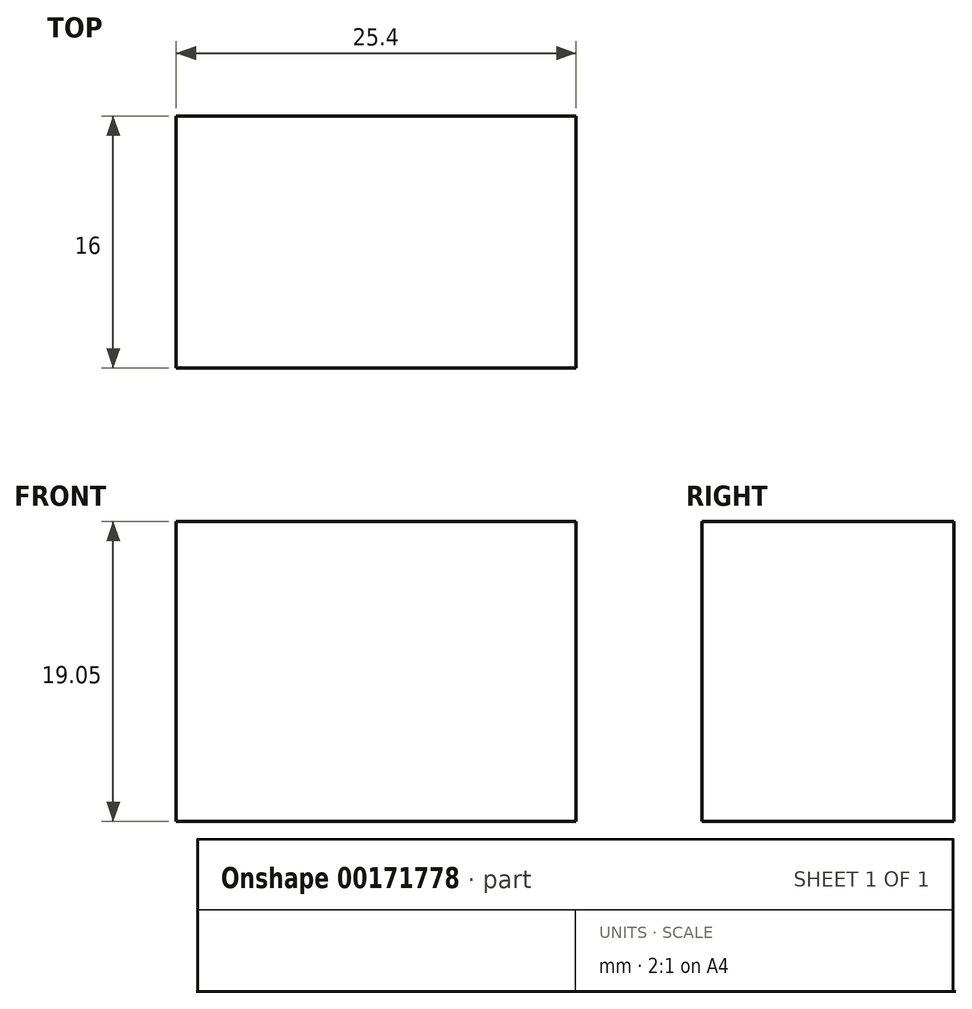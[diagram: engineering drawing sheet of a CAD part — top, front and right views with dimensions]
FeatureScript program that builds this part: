
annotation { "Feature Type Name" : "Feature", "Feature Type Description" : "" }
export const myFeature = defineFeature(function(context is Context, id is Id, definition is map)
    precondition{}
    {
        {
            var Q0;
            Q0=qCreatedBy(makeId("Front.planeOp"),FACE);
            var sketch = newSketch(context, id + "F0", { "sketchPlane" : qUnion([Q0])});
            skLineSegment(sketch, "E0.bottom", {"start": v(0, 0) * mm, "end": v(25.4, 0) * mm});
            skLineSegment(sketch, "E0.top", {"start": v(0, 19.05) * mm, "end": v(25.4, 19.05) * mm});
            skLineSegment(sketch, "E0.left", {"start": v(0, 0) * mm, "end": v(0, 19.05) * mm});
            skLineSegment(sketch, "E0.right", {"start": v(25.4, 0) * mm, "end": v(25.4, 19.05) * mm});
            skSolve(sketch);
        }
        {
            var Q0;
            Q0 = qSketchRegion(id + "F0", true);
            extrude(context, id + "F1", {"entities" : qUnion([Q0]), "depth" : 16 * mm});
        }
    });
